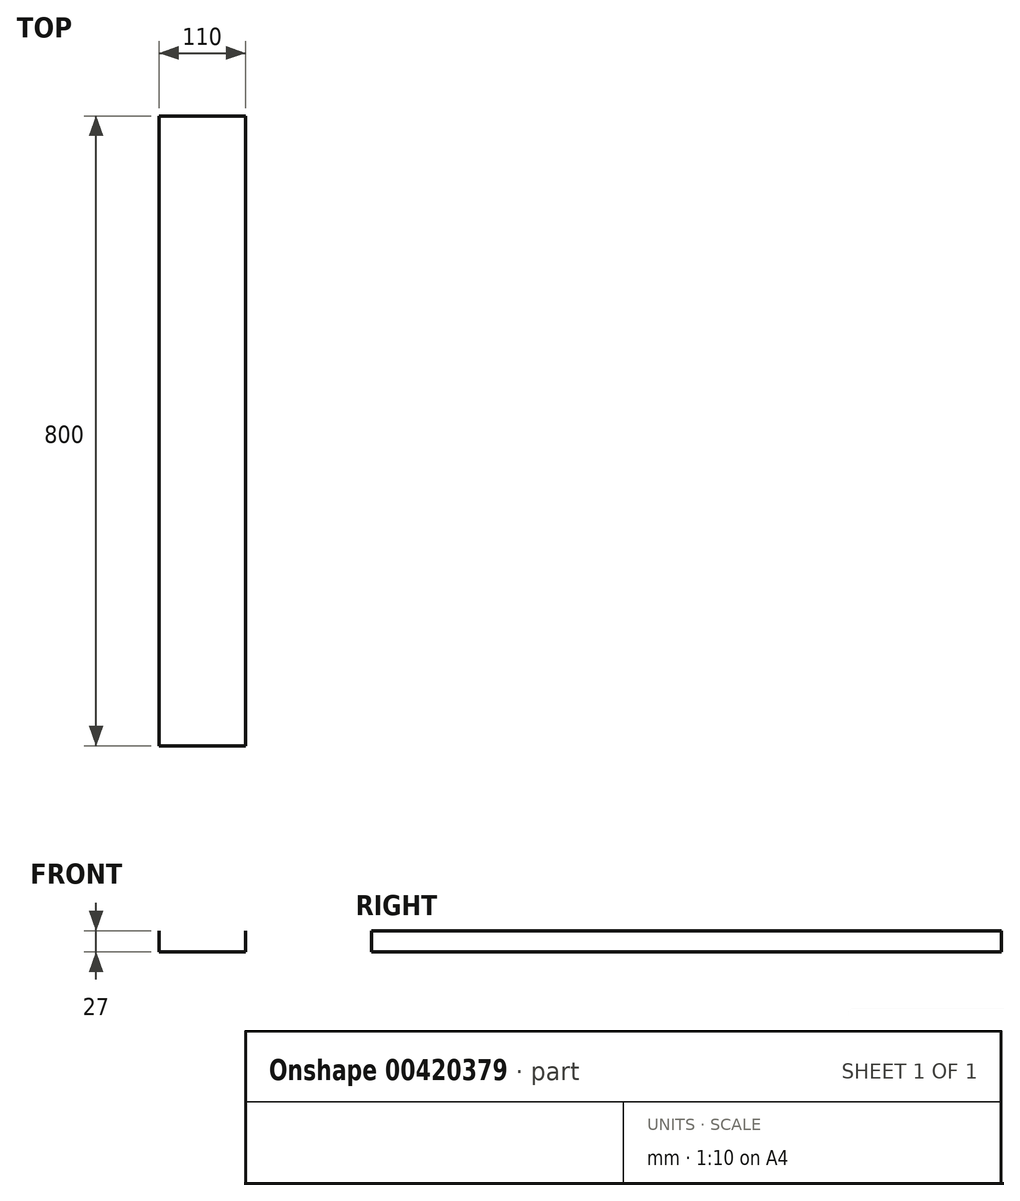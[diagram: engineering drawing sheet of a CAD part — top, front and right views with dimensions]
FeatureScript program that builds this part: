
annotation { "Feature Type Name" : "Feature", "Feature Type Description" : "" }
export const myFeature = defineFeature(function(context is Context, id is Id, definition is map)
    precondition{}
    {
        {
            var Q0;
            Q0=qCreatedBy(makeId("Front.planeOp"),FACE);
            var sketch = newSketch(context, id + "F0", { "sketchPlane" : qUnion([Q0])});
            skLineSegment(sketch, "E0.top", {"start": v(55, -13.5) * mm, "end": v(-55, -13.5) * mm});
            skLineSegment(sketch, "E0.left", {"start": v(55, 13.5) * mm, "end": v(55, -13.5) * mm});
            skLineSegment(sketch, "E0.right", {"start": v(-55, 13.5) * mm, "end": v(-55, -13.5) * mm});
            skPoint(sketch, "E0.middle", {"position": v(0, 0) * mm});
            skSolve(sketch);
        }
        {
            var Q0;
            Q0 = qSketchRegion(id + "F0", true);
            var Q1;
            Q1=sQuery(id+"F0.wireOp",EDGE,"E0.right");
            var Q2;
            Q2=sQuery(id+"F0.wireOp",EDGE,"E0.top");
            var Q3;
            Q3=sQuery(id+"F0.wireOp",EDGE,"E0.left");
            extrude(context, id + "F1", {"entities" : qUnion([Q0]), "bodyType" : ToolBodyType.SURFACE, "operationType" : NewBodyOperationType.ADD, "surfaceEntities" : qUnion([Q1, Q2, Q3]), "endBound" : BoundingType.SYMMETRIC, "depth" : 800 * mm});
        }
    });
